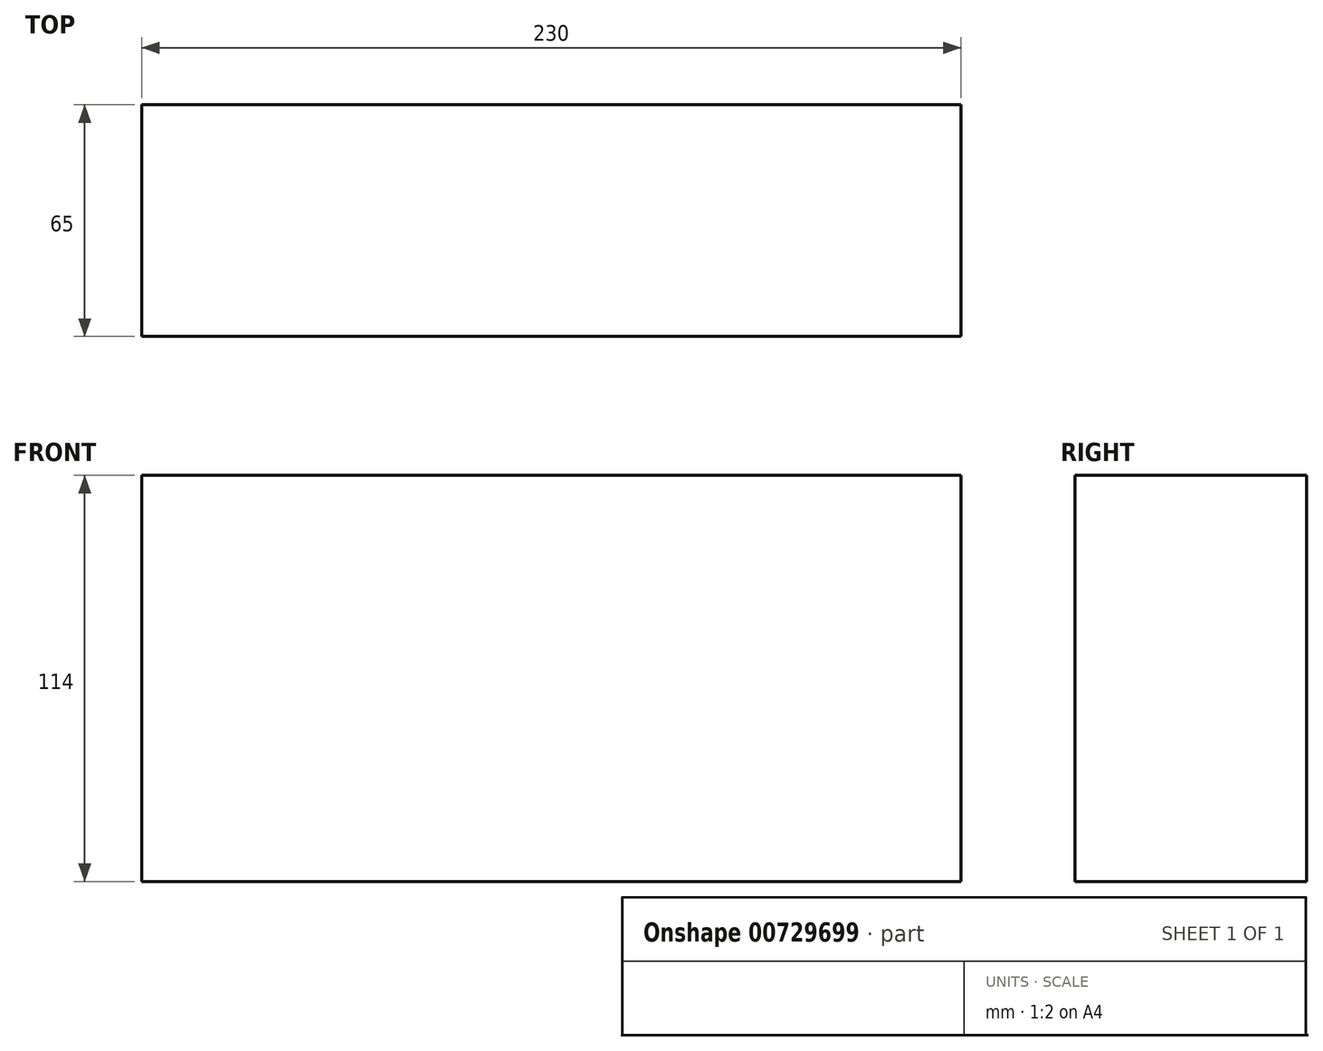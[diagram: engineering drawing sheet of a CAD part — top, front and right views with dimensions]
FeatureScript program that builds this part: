
annotation { "Feature Type Name" : "Feature", "Feature Type Description" : "" }
export const myFeature = defineFeature(function(context is Context, id is Id, definition is map)
    precondition{}
    {
        {
            var Q0;
            Q0=qCreatedBy(makeId("Front.planeOp"),FACE);
            var sketch = newSketch(context, id + "F0", { "sketchPlane" : qUnion([Q0])});
            skLineSegment(sketch, "E0.bottom", {"start": v(-79.26, -6.97) * mm, "end": v(150.74, -6.97) * mm});
            skLineSegment(sketch, "E0.top", {"start": v(-79.26, -120.97) * mm, "end": v(150.74, -120.97) * mm});
            skLineSegment(sketch, "E0.left", {"start": v(-79.26, -6.97) * mm, "end": v(-79.26, -120.97) * mm});
            skLineSegment(sketch, "E0.right", {"start": v(150.74, -6.97) * mm, "end": v(150.74, -120.97) * mm});
            skSolve(sketch);
        }
        {
            var Q0;
            Q0 = qSketchRegion(id + "F0", true);
            extrude(context, id + "F1", {"entities" : qUnion([Q0]), "depth" : 65 * mm, "offsetDistance" : 25 * mm});
        }
    });
